# Revit family: 73816XXX_NEW
name_source: partatom
category: Plumbing Fixtures
revit_build: Autodesk Revit 2018 (Build: 20170223_1515(x64)
units: mm (PartAtom-declared; Revit-internal decimal feet)

## family parameters
Always vertical = No
Cut with Voids When Loaded = No
OmniClass Number = 23.45.00.00
OmniClass Title = Sanitary, Laundry, and Cleaning Equipment
Part Type = Normal
Room Calculation Point = No
Round Connector Dimension = Use Diameter
Shared = No
Work Plane-Based = Yes

## types (2) — shared parameters
Always visible = Yes
BIMobject category = Taps & Mixers
Default Elevation = 1219 mm
Design country = Germany
EAN code = 4059625176221
Edition number = 1
GTIN code = https://4059625176221
IFC Classification = Sanitary Terminal
Installation instructions = https://www.hansgrohe.com
Manufacturer country = Germany
Manufacturer name = hansgrohe
Material main = Chrome
Material secondary = Chrome
Product Guid = 292296ee-4715-42df-92a4-aab47b1a3c76
Product SKU = 73816XXX
Product data url = https://www.bimobject.com
Product family = Metris Select M71
Product group = Kitchen mixers
Product name = 73816XXX Metris Select M71 Single lever kitchen mixer 320, pull-out spray, 2jet, sBox
Product url = https://www.hansgrohe.com
QR code = https://www.bimobject.com
Technical description = https://www.hansgrohe.com
Weight Net (Kg) = 4,3

## per-type parameters (varying)
| type | Material 1 |
| 800 Stainless Steel Optic | Hansgrohe - Metris Select - 800 Stainless Steel Optic |
| 000 Chrome | Hansgrohe - Metris Select - 000 Chrome |

## geometry (parser evidence)
native form markers: Sweep x2
no freeform markers — native parametric forms only
